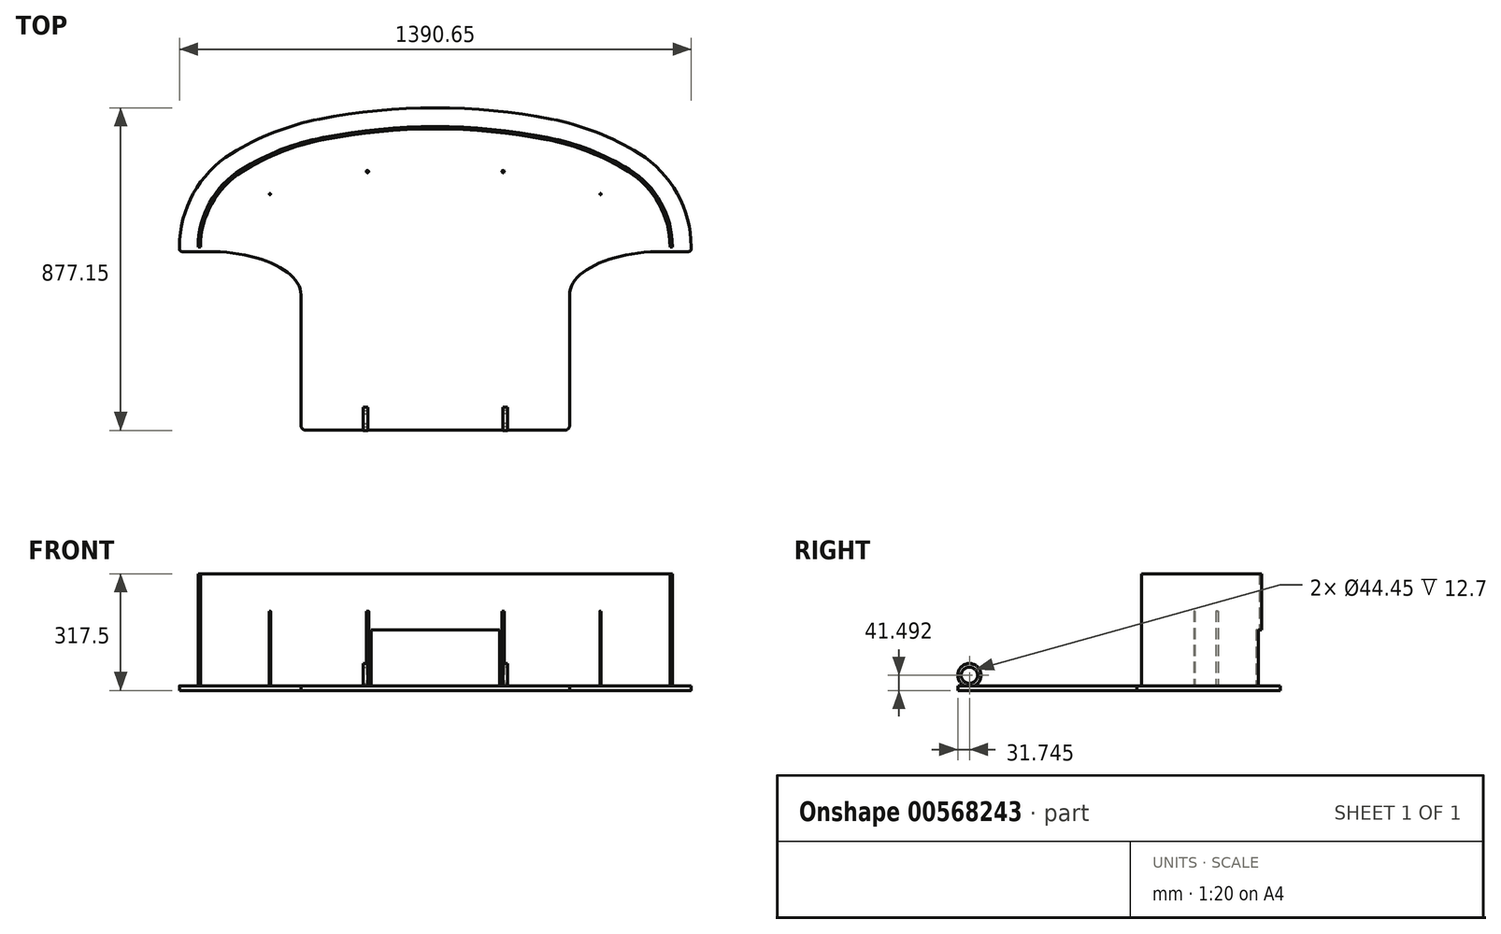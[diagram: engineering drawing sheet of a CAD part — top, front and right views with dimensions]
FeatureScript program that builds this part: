
annotation { "Feature Type Name" : "Feature", "Feature Type Description" : "" }
export const myFeature = defineFeature(function(context is Context, id is Id, definition is map)
    precondition{}
    {
        {
            var Q0;
            Q0=qCreatedBy(makeId("Top.planeOp"),FACE);
            var sketch = newSketch(context, id + "F0", { "sketchPlane" : qUnion([Q0])});
            skArc(sketch, "E0", {"start": v(-599.05, 40.59) * mm, "mid": v(-597.19, 36.1) * mm, "end": v(-592.7, 34.24) * mm});
            skArc(sketch, "E1", {"start": v(785.25, 34.24) * mm, "mid": v(789.74, 36.1) * mm, "end": v(791.6, 40.59) * mm});
            skArc(sketch, "E2", {"start": v(-268.85, -438.84) * mm, "mid": v(-265.13, -447.82) * mm, "end": v(-256.15, -451.54) * mm});
            skArc(sketch, "E3", {"start": v(448.7, -451.54) * mm, "mid": v(457.68, -447.82) * mm, "end": v(461.4, -438.84) * mm});
            skLineSegment(sketch, "E4", {"start": v(-268.85, -83.24) * mm, "end": v(-268.85, -438.84) * mm});
            skLineSegment(sketch, "E5", {"start": v(-256.15, -451.54) * mm, "end": v(448.7, -451.54) * mm});
            skLineSegment(sketch, "E6", {"start": v(461.4, -438.84) * mm, "end": v(461.4, -83.24) * mm});
            skEllipticalArc(sketch, "E7", {});
            skLineSegment(sketch, "E8", {"start": v(715.4, 34.24) * mm, "end": v(785.25, 34.24) * mm});
            skLineSegment(sketch, "E9", {"start": v(791.6, 40.59) * mm, "end": v(791.6, 46.94) * mm});
            skArc(sketch, "E10", {"start": v(791.6, 46.94) * mm, "mid": v(754, 191.96) * mm, "end": v(650.66, 300.44) * mm});
            skArc(sketch, "E11", {"start": v(650.66, 300.44) * mm, "mid": v(535.03, 358.44) * mm, "end": v(410.81, 394.53) * mm});
            skArc(sketch, "E12", {"start": v(410.81, 394.53) * mm, "mid": v(96.28, 424.76) * mm, "end": v(-218.26, 394.53) * mm});
            skArc(sketch, "E13", {"start": v(-218.26, 394.53) * mm, "mid": v(-342.48, 358.44) * mm, "end": v(-458.1, 300.44) * mm});
            skArc(sketch, "E14", {"start": v(-458.1, 300.44) * mm, "mid": v(-561.44, 191.96) * mm, "end": v(-599.05, 46.94) * mm});
            skLineSegment(sketch, "E15", {"start": v(-599.05, 46.94) * mm, "end": v(-599.05, 40.59) * mm});
            skLineSegment(sketch, "E16", {"start": v(-592.7, 34.24) * mm, "end": v(-522.85, 34.24) * mm});
            skEllipticalArc(sketch, "E17", {});
            const initialGuessF0  = {"E7": [0.7154011092000001, -0.08323519039999995, -10, 0, 0.254, 0.117475, 4.712389, 6.283185], "E17": [-0.5228488908, -0.08323519039999995, 10, 0, 0.254, 0.117475, 0, 1.570796]};
            skSetInitialGuess(sketch, initialGuessF0);
            skSolve(sketch);
        }
        {
            var Q0;
            Q0=makeQuery(id+"F0.imprint","IMPRINT",FACE,{"disambiguationData":[TD([[makeQuery(id+"F0.imprint","IMPRINT",EDGE,{"derivedFrom":sQuery(id+"F0.wireOp",EDGE,"E0")}),1.0]])]});
            extrude(context, id + "F1", {"entities" : qUnion([Q0]), "depth" : 12.7 * mm, "offsetDistance" : 25.4 * mm});
        }
        {
            var Q0;
            Q0=qCreatedBy(makeId("Right.planeOp"),FACE);
            cPlane(context, id + "F2", {"entities" : qUnion([Q0]), "cplaneType" : CPlaneType.OFFSET, "offset" : 279.4 * mm, "width" : 152.4 * mm, "height" : 152.4 * mm});
        }
        {
            var Q0;
            Q0=qCreatedBy(id+"F2.planeOp",FACE);
            var sketch = newSketch(context, id + "F3", { "sketchPlane" : qUnion([Q0])});
            skCircle(sketch, "E18", {"center": v(-420.64, 41.5) * mm, "radius": 22.23 * mm});
            skCircle(sketch, "E19", {"center": v(-420.64, 41.5) * mm, "radius": 31.75 * mm});
            skSolve(sketch);
        }
        {
            var Q0;
            Q0=makeQuery(id+"F3.imprint","IMPRINT",FACE,{"disambiguationData":[TD([[makeQuery(id+"F3.imprint","IMPRINT",EDGE,{"derivedFrom":sQuery(id+"F3.wireOp",EDGE,"E18")}),-1.0]])]});
            extrude(context, id + "F4", {"entities" : qUnion([Q0]), "operationType" : NewBodyOperationType.ADD, "depth" : 12.7 * mm, "offsetDistance" : 25.4 * mm});
        }
        {
            var Q0;
            Q0=makeQuery(id+"F1.opExtrude","CAP_FACE",FACE,{"disambiguationData":[OSD([sQuery(id+"F0.wireOp",EDGE,"E0"),sQuery(id+"F0.wireOp",EDGE,"E1"),sQuery(id+"F0.wireOp",EDGE,"E2"),sQuery(id+"F0.wireOp",EDGE,"E3"),sQuery(id+"F0.wireOp",EDGE,"E4"),sQuery(id+"F0.wireOp",EDGE,"E5"),sQuery(id+"F0.wireOp",EDGE,"E6"),sQuery(id+"F0.wireOp",EDGE,"E7"),sQuery(id+"F0.wireOp",EDGE,"E8"),sQuery(id+"F0.wireOp",EDGE,"E9"),sQuery(id+"F0.wireOp",EDGE,"E10"),sQuery(id+"F0.wireOp",EDGE,"E11"),sQuery(id+"F0.wireOp",EDGE,"E12"),sQuery(id+"F0.wireOp",EDGE,"E13"),sQuery(id+"F0.wireOp",EDGE,"E14"),sQuery(id+"F0.wireOp",EDGE,"E15"),sQuery(id+"F0.wireOp",EDGE,"E16"),sQuery(id+"F0.wireOp",EDGE,"E17")])],"isStart":false});
            var sketch = newSketch(context, id + "F5", { "sketchPlane" : qUnion([Q0])});
            skCircle(sketch, "E20", {"center": v(280.7, 252.01) * mm, "radius": 3.18 * mm});
            skCircle(sketch, "E21", {"center": v(545.54, 190.6) * mm, "radius": 1.59 * mm});
            skSolve(sketch);
        }
        {
            var Q0;
            Q0=makeQuery(id+"F5.imprint","IMPRINT",FACE,{"disambiguationData":[TD([[makeQuery(id+"F5.imprint","IMPRINT",EDGE,{"derivedFrom":sQuery(id+"F5.wireOp",EDGE,"E21")}),1.0]])]});
            var Q1;
            Q1=makeQuery(id+"F5.imprint","IMPRINT",FACE,{"disambiguationData":[TD([[makeQuery(id+"F5.imprint","IMPRINT",EDGE,{"derivedFrom":sQuery(id+"F5.wireOp",EDGE,"E20")}),1.0]])]});
            extrude(context, id + "F6", {"entities" : qUnion([Q0, Q1]), "operationType" : NewBodyOperationType.ADD, "depth" : 203.2 * mm, "offsetDistance" : 25.4 * mm});
        }
        {
            var Q0;
            Q0=makeQuery(id+"F1.opExtrude","SWEPT_FACE",FACE,{"disambiguationData":[OSD([sQuery(id+"F0.wireOp",EDGE,"E6")])]});
            cPlane(context, id + "F7", {"entities" : qUnion([Q0]), "cplaneType" : CPlaneType.OFFSET, "offset" : 365.12 * mm, "oppositeDirection" : true, "width" : 152.4 * mm, "height" : 152.4 * mm});
        }
        {
            var Q0;
            Q0=makeQuery(id+"F1.opExtrude","SWEPT_BODY",BODY,{"disambiguationData":[OSD([sQuery(id+"F0.wireOp",EDGE,"E0"),sQuery(id+"F0.wireOp",EDGE,"E1"),sQuery(id+"F0.wireOp",EDGE,"E2"),sQuery(id+"F0.wireOp",EDGE,"E3"),sQuery(id+"F0.wireOp",EDGE,"E4"),sQuery(id+"F0.wireOp",EDGE,"E5"),sQuery(id+"F0.wireOp",EDGE,"E6"),sQuery(id+"F0.wireOp",EDGE,"E7"),sQuery(id+"F0.wireOp",EDGE,"E8"),sQuery(id+"F0.wireOp",EDGE,"E9"),sQuery(id+"F0.wireOp",EDGE,"E10"),sQuery(id+"F0.wireOp",EDGE,"E11"),sQuery(id+"F0.wireOp",EDGE,"E12"),sQuery(id+"F0.wireOp",EDGE,"E13"),sQuery(id+"F0.wireOp",EDGE,"E14"),sQuery(id+"F0.wireOp",EDGE,"E15"),sQuery(id+"F0.wireOp",EDGE,"E16"),sQuery(id+"F0.wireOp",EDGE,"E17")])]});
            var Q1;
            Q1=qCreatedBy(id+"F7.planeOp",FACE);
            mirror(context, id + "F8", {"operationType" : NewBodyOperationType.ADD, "entities" : qUnion([Q0]), "mirrorPlane" : qUnion([Q1])});
        }
        {
            var Q0;
            Q0=makeQuery(id+"F1.opExtrude","CAP_FACE",FACE,{"disambiguationData":[OSD([sQuery(id+"F0.wireOp",EDGE,"E0"),sQuery(id+"F0.wireOp",EDGE,"E1"),sQuery(id+"F0.wireOp",EDGE,"E2"),sQuery(id+"F0.wireOp",EDGE,"E3"),sQuery(id+"F0.wireOp",EDGE,"E4"),sQuery(id+"F0.wireOp",EDGE,"E5"),sQuery(id+"F0.wireOp",EDGE,"E6"),sQuery(id+"F0.wireOp",EDGE,"E7"),sQuery(id+"F0.wireOp",EDGE,"E8"),sQuery(id+"F0.wireOp",EDGE,"E9"),sQuery(id+"F0.wireOp",EDGE,"E10"),sQuery(id+"F0.wireOp",EDGE,"E11"),sQuery(id+"F0.wireOp",EDGE,"E12"),sQuery(id+"F0.wireOp",EDGE,"E13"),sQuery(id+"F0.wireOp",EDGE,"E14"),sQuery(id+"F0.wireOp",EDGE,"E15"),sQuery(id+"F0.wireOp",EDGE,"E16"),sQuery(id+"F0.wireOp",EDGE,"E17")])],"isStart":false});
            var sketch = newSketch(context, id + "F9", { "sketchPlane" : qUnion([Q0])});
            skArc(sketch, "E22.0", {"start": v(740.8, 46.94) * mm, "mid": v(709.6, 167.28) * mm, "end": v(623.85, 257.3) * mm});
            skArc(sketch, "E23.0", {"start": v(623.85, 257.3) * mm, "mid": v(516.48, 311.14) * mm, "end": v(401.13, 344.66) * mm});
            skArc(sketch, "E24.0", {"start": v(401.13, 344.66) * mm, "mid": v(96.28, 373.96) * mm, "end": v(-208.58, 344.66) * mm});
            skArc(sketch, "E25.0", {"start": v(-208.58, 344.66) * mm, "mid": v(-323.93, 311.14) * mm, "end": v(-431.3, 257.3) * mm});
            skArc(sketch, "E26.0", {"start": v(-431.3, 257.3) * mm, "mid": v(-517.05, 167.28) * mm, "end": v(-548.25, 46.94) * mm});
            skArc(sketch, "E27.0", {"start": v(734.45, 46.94) * mm, "mid": v(704.05, 164.2) * mm, "end": v(620.5, 251.9) * mm});
            skArc(sketch, "E28.0", {"start": v(620.5, 251.9) * mm, "mid": v(514.16, 305.23) * mm, "end": v(399.92, 338.42) * mm});
            skArc(sketch, "E29.0", {"start": v(399.92, 338.42) * mm, "mid": v(96.28, 367.61) * mm, "end": v(-207.37, 338.42) * mm});
            skArc(sketch, "E30.0", {"start": v(-207.37, 338.42) * mm, "mid": v(-321.6, 305.23) * mm, "end": v(-427.95, 251.9) * mm});
            skArc(sketch, "E31.0", {"start": v(-427.95, 251.9) * mm, "mid": v(-511.5, 164.2) * mm, "end": v(-541.9, 46.94) * mm});
            skLineSegment(sketch, "E32", {"start": v(740.8, 46.94) * mm, "end": v(734.45, 46.94) * mm});
            skLineSegment(sketch, "E33", {"start": v(-541.9, 46.94) * mm, "end": v(-548.25, 46.94) * mm});
            skSolve(sketch);
        }
        {
            var Q0;
            Q0=makeQuery(id+"F9.imprint","IMPRINT",FACE,{"disambiguationData":[TD([[makeQuery(id+"F9.imprint","IMPRINT",EDGE,{"derivedFrom":sQuery(id+"F9.wireOp",EDGE,"E22.0")}),1.0]])]});
            extrude(context, id + "F10", {"entities" : qUnion([Q0]), "operationType" : NewBodyOperationType.ADD, "depth" : 304.8 * mm, "offsetDistance" : 25.4 * mm});
        }
        {
            var Q0;
            Q0=makeQuery(id+"F1.opExtrude","SWEPT_FACE",FACE,{"disambiguationData":[OSD([sQuery(id+"F0.wireOp",EDGE,"E5")])]});
            var sketch = newSketch(context, id + "F11", { "sketchPlane" : qUnion([Q0])});
            skLineSegment(sketch, "E34.bottom", {"start": v(-78.35, 12.7) * mm, "end": v(270.9, 12.7) * mm});
            skLineSegment(sketch, "E34.top", {"start": v(-78.35, 165.1) * mm, "end": v(270.9, 165.1) * mm});
            skLineSegment(sketch, "E34.left", {"start": v(-78.35, 12.7) * mm, "end": v(-78.35, 165.1) * mm});
            skLineSegment(sketch, "E34.right", {"start": v(270.9, 12.7) * mm, "end": v(270.9, 165.1) * mm});
            skSolve(sketch);
        }
        {
            var Q0;
            Q0=makeQuery(id+"F11.imprint","IMPRINT",FACE,{"disambiguationData":[TD([[makeQuery(id+"F11.imprint","IMPRINT",EDGE,{"derivedFrom":sQuery(id+"F11.wireOp",EDGE,"E34.bottom")}),1.0]])]});
            extrude(context, id + "F12", {"entities" : qUnion([Q0]), "operationType" : NewBodyOperationType.REMOVE, "endBound" : BoundingType.THROUGH_ALL, "oppositeDirection" : true, "depth" : 25.4 * mm, "offsetDistance" : 25.4 * mm});
        }
    });
